# Revit family: ROTHOB_Rothoblaas_Membrane_BarrierAluNetAdhesive300
name_source: partatom
category: Structural Connections
units: mm (PartAtom-declared; Revit-internal decimal feet)

## family parameters
Cut with Voids When Loaded = No
Enable cutting in views = Yes
Host = Face
Material for Model Behavior = Other
OmniClass Number = 23.13.25.25
OmniClass Title = Air Barriers
Shared = No

## types (1)
- BARRIER ALU NET ADHESIVE 300
    BIMObjectName = ROTHOB_Rothoblaas_Membrane_BarrierAluNetAdhesive300
    CECode = EN 13984
    Category = Pr_25_57_65_63 - Polyethylene sheets
    CodePerformance = CE - Construction products
    Color = Grey
    Default Elevation = 1.22 m
    Description = Self-adhesive reflective vapour barrier
    DurationUnit = Years
    Esporta tipo in formato IFC con nome = IfcCoveringType.MEMBRANE
    Features = Flexible sheets for waterproofing - Plastic and rubber vapour control layers
    Finish = Aluminium film with PET film protection
    IfcExportAs = IfcCoveringType.MEMBRANE
    IfcExportType = USERDEFINED
    ManufacturerName = ROTHO BLAAS SRL
    ManufacturerURL = www.rothoblaas.com
    MassUnitArea = 300 g/m2
    Material = Aluminium and polyethylene
    ModelDisclaimer = The latest version of the data sheets can be found on our website
    Name = Membrane
    ObjectMaterial = ROTHOB_Rothoblaas_Aluminium_Polyethylene
    OmniClassCode = 23.13.25.25
    OmniClassTitle = Air Barriers
    OmniClassVersion = 2012-05-16
    ProductInformation = https://www.rothoblaas.com
    RadonDiffusionCoefficient_D = < 3,5 e-15 m2/s
    RadonDiffusionLength_l = < 0,000041 m
    ReactionFire = class B-s1, d0
    Shape = Bidimensional
    Tipo IFC predefinito = USERDEFINED
    UniClass2015Code = Pr_25_57_65_63
    UniClass2015Title = Polyethylene sheets
    UniClass2015Version = Products v1.33
    Version = 1
    WaterVapourTransmition_Sd = 4000 m
